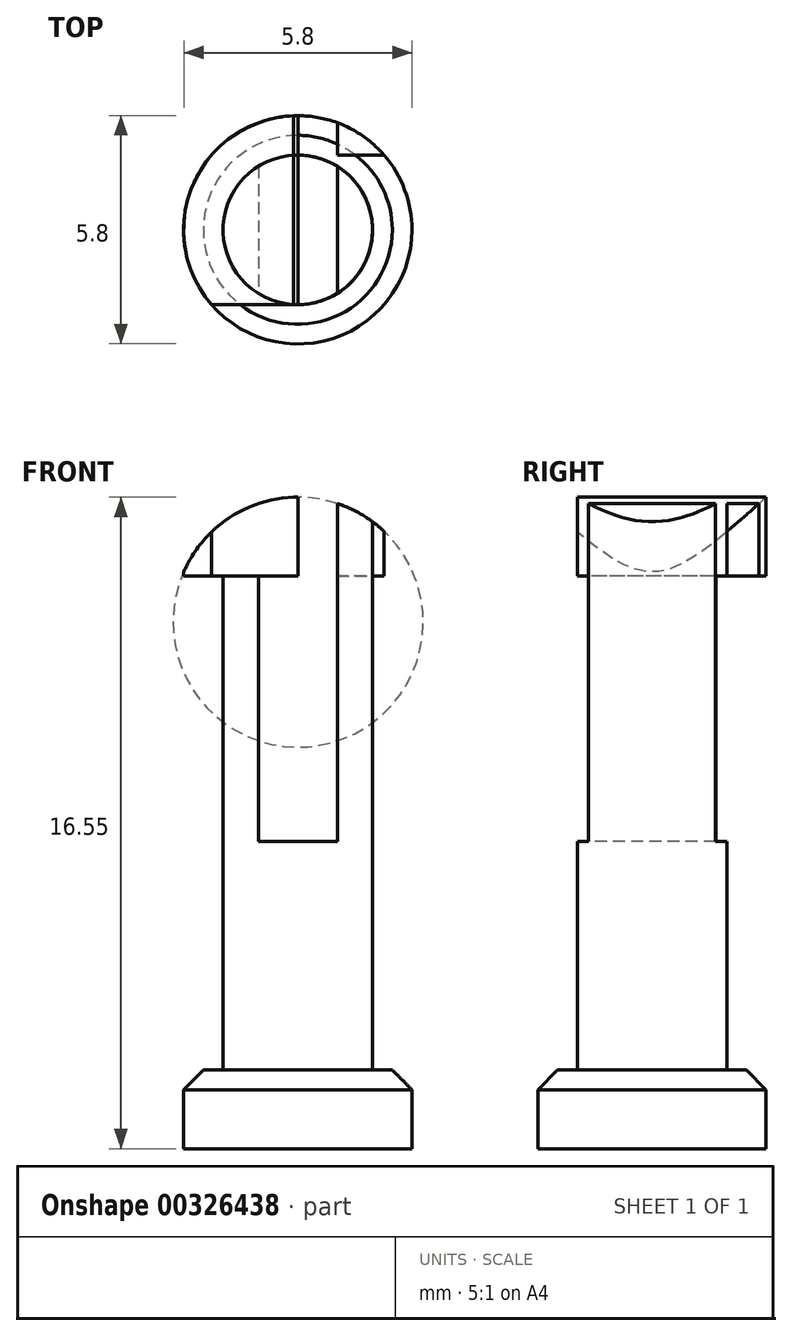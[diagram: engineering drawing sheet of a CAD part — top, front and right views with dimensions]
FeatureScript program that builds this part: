
annotation { "Feature Type Name" : "Feature", "Feature Type Description" : "" }
export const myFeature = defineFeature(function(context is Context, id is Id, definition is map)
    precondition{}
    {
        {
            var Q0;
            Q0=qCreatedBy(makeId("Top.planeOp"),FACE);
            var sketch = newSketch(context, id + "F0", { "sketchPlane" : qUnion([Q0])});
            skCircle(sketch, "E0", {"center": v(-52.06, 27.8) * mm, "radius": 2.9 * mm});
            skSolve(sketch);
        }
        {
            var Q0;
            Q0=makeQuery(id+"F0.imprint","IMPRINT",FACE,{"disambiguationData":[TD([[makeQuery(id+"F0.imprint","IMPRINT",EDGE,{"derivedFrom":sQuery(id+"F0.wireOp",EDGE,"E0")}),1.0]])]});
            extrude(context, id + "F1", {"entities" : qUnion([Q0]), "depth" : 2 * mm});
        }
        {
            var Q0;
            Q0=makeQuery(id+"F1.opExtrude","CAP_FACE",FACE,{"disambiguationData":[OSD([sQuery(id+"F0.wireOp",EDGE,"E0")])],"isStart":false});
            var sketch = newSketch(context, id + "F2", { "sketchPlane" : qUnion([Q0])});
            skPoint(sketch, "E1", {"position": v(-52.06, 27.8) * mm});
            skCircle(sketch, "E2", {"center": v(-52.06, 27.8) * mm, "radius": 1.9 * mm});
            skSolve(sketch);
        }
        {
            var Q0;
            Q0=makeQuery(id+"F2.imprint","IMPRINT",FACE,{"disambiguationData":[TD([[makeQuery(id+"F2.imprint","IMPRINT",EDGE,{"derivedFrom":sQuery(id+"F2.wireOp",EDGE,"E2")}),1.0]])]});
            var Q1;
            Q1=sQuery(id+"F2.wireOp",EDGE,"E2");
            extrude(context, id + "F3", {"entities" : qUnion([Q0]), "operationType" : NewBodyOperationType.ADD, "surfaceEntities" : qUnion([Q1]), "depth" : 12.55 * mm});
        }
        {
            var Q0;
            Q0=makeQuery(id+"F3.opExtrude","CAP_FACE",FACE,{"disambiguationData":[OSD([sQuery(id+"F2.wireOp",EDGE,"E2")])],"isStart":false});
            var sketch = newSketch(context, id + "F4", { "sketchPlane" : qUnion([Q0])});
            skPoint(sketch, "E3", {"position": v(-52.06, 27.8) * mm});
            skCircle(sketch, "E4", {"center": v(-52.06, 27.8) * mm, "radius": 2.9 * mm});
            skLineSegment(sketch, "E5", {"start": v(-52.06, 30.7) * mm, "end": v(-52.06, 24.9) * mm, "construction": true});
            skLineSegment(sketch, "E6", {"start": v(-52.06, 29.7) * mm, "end": v(-49.87, 29.7) * mm});
            skLineSegment(sketch, "E7", {"start": v(-49.87, 29.7) * mm, "end": v(-54.26, 29.7) * mm});
            skLineSegment(sketch, "E8", {"start": v(-52.06, 25.9) * mm, "end": v(-49.87, 25.9) * mm});
            skLineSegment(sketch, "E9", {"start": v(-49.87, 25.9) * mm, "end": v(-54.26, 25.9) * mm});
            skSolve(sketch);
        }
        {
            var Q0;
            {var subQ0=sQuery(id+"F4.wireOp",EDGE,"E7");var subQ1=sQuery(id+"F4.wireOp",EDGE,"E4");var subQ2=makeQuery(id+"F4.imprint","INTERSECT",VERTEX,{"disambiguationData":[OD(1.0)],"derivedFrom":[subQ1,subQ0]});Q0=makeQuery(id+"F4.imprint","IMPRINT",FACE,{"disambiguationData":[TD([[makeQuery(id+"F4.imprint","IMPRINT",EDGE,{"disambiguationData":[TD([[subQ2,-1.0]])],"derivedFrom":subQ1}),1.0]])]});}
            var Q1;
            {var subQ0=makeQuery(id+"F3.opExtrude","CAP_EDGE",EDGE,{"disambiguationData":[OSD([sQuery(id+"F2.wireOp",EDGE,"E2")])],"isStart":false});var subQ1=makeQuery(id+"F4.imprint","INTERSECT",VERTEX,{"derivedFrom":[subQ0,sQuery(id+"F4.wireOp",EDGE,"E7")]});Q1=makeQuery(id+"F4.imprint","IMPRINT",FACE,{"disambiguationData":[TD([[makeQuery(id+"F4.imprint","IMPRINT",EDGE,{"disambiguationData":[TD([[subQ1,-1.0]])],"derivedFrom":subQ0}),1.0]])]});}
            var Q2;
            {var subQ0=sQuery(id+"F4.wireOp",EDGE,"E7");var subQ1=sQuery(id+"F4.wireOp",EDGE,"E4");var subQ2=makeQuery(id+"F4.imprint","INTERSECT",VERTEX,{"disambiguationData":[OD(0.0)],"derivedFrom":[subQ1,subQ0]});Q2=makeQuery(id+"F4.imprint","IMPRINT",FACE,{"disambiguationData":[TD([[makeQuery(id+"F4.imprint","IMPRINT",EDGE,{"disambiguationData":[TD([[subQ2,1.0]])],"derivedFrom":subQ1}),1.0]])]});}
            extrude(context, id + "F5", {"entities" : qUnion([Q0, Q1, Q2]), "operationType" : NewBodyOperationType.ADD, "depth" : 2 * mm});
        }
        {
            var Q0;
            Q0=makeQuery(id+"F5.opExtrude","SWEPT_FACE",FACE,{"disambiguationData":[OSD([sQuery(id+"F4.wireOp",EDGE,"E9")])]});
            var sketch = newSketch(context, id + "F6", { "sketchPlane" : qUnion([Q0])});
            skLineSegment(sketch, "E10.bottom", {"start": v(-55, 16.55) * mm, "end": v(-49.1, 16.55) * mm});
            skLineSegment(sketch, "E10.top", {"start": v(-55, 14.55) * mm, "end": v(-53.06, 14.55) * mm});
            skLineSegment(sketch, "E10.left", {"start": v(-55, 16.55) * mm, "end": v(-55, 14.55) * mm});
            skLineSegment(sketch, "E10.right", {"start": v(-49.1, 16.55) * mm, "end": v(-49.1, 14.55) * mm});
            skPoint(sketch, "E11", {"position": v(-52.06, 16.55) * mm});
            skArc(sketch, "E12", {"start": v(-49.1, 14.55) * mm, "mid": v(-52.06, 16.55) * mm, "end": v(-55, 14.55) * mm});
            skPoint(sketch, "E13", {"position": v(-52.06, 2) * mm});
            skLineSegment(sketch, "E14", {"start": v(-52.06, 2) * mm, "end": v(-52.06, 14.55) * mm, "construction": true});
            skLineSegment(sketch, "E15.top", {"start": v(-53.06, 7.8) * mm, "end": v(-51.06, 7.8) * mm});
            skLineSegment(sketch, "E15.left", {"start": v(-53.06, 14.55) * mm, "end": v(-53.06, 7.8) * mm});
            skLineSegment(sketch, "E15.right", {"start": v(-51.06, 13.8) * mm, "end": v(-51.06, 7.8) * mm});
            skPoint(sketch, "E16", {"position": v(-52.06, 7.8) * mm});
            skLineSegment(sketch, "E17", {"start": v(-53.06, 14.55) * mm, "end": v(-53.06, 16.55) * mm});
            skLineSegment(sketch, "E18", {"start": v(-51.06, 13.8) * mm, "end": v(-51.06, 16.55) * mm});
            skLineSegment(sketch, "E19.trimOffspring", {"start": v(-51.06, 14.55) * mm, "end": v(-49.1, 14.55) * mm});
            skSolve(sketch);
        }
        {
            var Q0;
            {var subQ0=sQuery(id+"F6.wireOp",EDGE,"XV074B50-gbtO-xtoO-LmDx-LcEMkbkd0Xud.bottom");var subQ1=makeQuery(id+"F6.imprint","IMPRINT",VERTEX,{"derivedFrom":subQ0});var subQ4=sQuery(id+"F6.wireOp",EDGE,"E17");var subQ5=makeQuery(id+"F6.imprint","INTERSECT",VERTEX,{"derivedFrom":[subQ0,sQuery(id+"F6.wireOp",EDGE,"E15.left"),subQ4]});Q0=makeQuery(id+"F6.imprint","IMPRINT",FACE,{"disambiguationData":[TD([[makeQuery(id+"F6.imprint","IMPRINT",EDGE,{"disambiguationData":[TD([[subQ1,1.0],[subQ5,-1.0]])],"derivedFrom":subQ0}),1.0]])]});}
            var Q1;
            {var subQ0=sQuery(id+"F6.wireOp",EDGE,"E12");var subQ4=sQuery(id+"F6.wireOp",EDGE,"E17");var subQ5=makeQuery(id+"F6.imprint","INTERSECT",VERTEX,{"derivedFrom":[subQ0,subQ4]});Q1=makeQuery(id+"F6.imprint","IMPRINT",FACE,{"disambiguationData":[TD([[makeQuery(id+"F6.imprint","IMPRINT",EDGE,{"disambiguationData":[TD([[subQ5,1.0]])],"derivedFrom":subQ0}),-1.0]])]});}
            var Q2;
            {var subQ0=sQuery(id+"F6.wireOp",EDGE,"E18");var subQ1=sQuery(id+"F6.wireOp",EDGE,"E12");var subQ2=makeQuery(id+"F6.imprint","INTERSECT",VERTEX,{"derivedFrom":[subQ1,subQ0]});Q2=makeQuery(id+"F6.imprint","IMPRINT",FACE,{"disambiguationData":[TD([[makeQuery(id+"F6.imprint","IMPRINT",EDGE,{"disambiguationData":[TD([[subQ2,-1.0]])],"derivedFrom":subQ1}),-1.0]])]});}
            var Q3;
            {var subQ0=sQuery(id+"F6.wireOp",EDGE,"E18");var subQ1=sQuery(id+"F6.wireOp",EDGE,"E12");var subQ2=makeQuery(id+"F6.imprint","INTERSECT",VERTEX,{"derivedFrom":[subQ1,subQ0]});Q3=makeQuery(id+"F6.imprint","IMPRINT",FACE,{"disambiguationData":[TD([[makeQuery(id+"F6.imprint","IMPRINT",EDGE,{"disambiguationData":[TD([[subQ2,-1.0]])],"derivedFrom":subQ0}),-1.0]])]});}
            var Q4;
            {var subQ1=sQuery(id+"F6.wireOp",EDGE,"E10.right");Q4=makeQuery(id+"F6.imprint","IMPRINT",FACE,{"disambiguationData":[TD([[makeQuery(id+"F6.imprint","IMPRINT",EDGE,{"derivedFrom":subQ1}),-1.0]])]});}
            var Q5;
            {var subQ0=sQuery(id+"F6.wireOp",EDGE,"E17");var subQ1=sQuery(id+"F6.wireOp",EDGE,"E12");var subQ2=makeQuery(id+"F6.imprint","INTERSECT",VERTEX,{"derivedFrom":[subQ1,subQ0]});Q5=makeQuery(id+"F6.imprint","IMPRINT",FACE,{"disambiguationData":[TD([[makeQuery(id+"F6.imprint","IMPRINT",EDGE,{"disambiguationData":[TD([[subQ2,-1.0]])],"derivedFrom":subQ0}),1.0]])]});}
            var Q6;
            {var subQ7=sQuery(id+"F6.wireOp",EDGE,"E10.left");Q6=makeQuery(id+"F6.imprint","IMPRINT",FACE,{"disambiguationData":[TD([[makeQuery(id+"F6.imprint","IMPRINT",EDGE,{"derivedFrom":subQ7}),1.0]])]});}
            var Q7;
            Q7=makeQuery(id+"F6.imprint","IMPRINT",FACE,{"disambiguationData":[TD([[makeQuery(id+"F6.imprint","IMPRINT",EDGE,{"derivedFrom":sQuery(id+"F6.wireOp",EDGE,"E15.top")}),1.0]])]});
            var Q8;
            Q8=makeQuery(id+"F5.opExtrude","SWEPT_FACE",FACE,{"disambiguationData":[OSD([sQuery(id+"F4.wireOp",EDGE,"E7")])]});
            extrude(context, id + "F7", {"entities" : qUnion([Q0, Q1, Q2, Q3, Q4, Q5, Q6, Q7, Q8]), "operationType" : NewBodyOperationType.REMOVE, "oppositeDirection" : true, "depth" : 25 * mm});
        }
        {
            var Q0;
            Q0=makeQuery(id+"F1.opExtrude","CAP_EDGE",EDGE,{"disambiguationData":[OSD([sQuery(id+"F0.wireOp",EDGE,"E0")])],"isStart":false});
            chamfer(context, id + "F8", {"entities" : qUnion([Q0]), "width" : 0.5 * mm, "tangentPropagation" : true});
        }
        {
            var Q0;
            {var subQ13=sQuery(id+"F6.wireOp",EDGE,"E12");var subQ17=sQuery(id+"F6.wireOp",EDGE,"E18");var subQ18=makeQuery(id+"F6.imprint","INTERSECT",VERTEX,{"derivedFrom":[subQ13,subQ17]});Q0=makeQuery(id+"F6.imprint","IMPRINT",FACE,{"disambiguationData":[TD([[makeQuery(id+"F6.imprint","IMPRINT",EDGE,{"disambiguationData":[TD([[subQ18,-1.0]])],"derivedFrom":subQ13}),1.0]])]});}
            var Q1;
            Q1=makeQuery(id+"F6.imprint","IMPRINT",FACE,{"disambiguationData":[TD([[makeQuery(id+"F6.imprint","IMPRINT",EDGE,{"derivedFrom":sQuery(id+"F6.wireOp",EDGE,"E15.top")}),1.0]])]});
            extrude(context, id + "F9", {"entities" : qUnion([Q0, Q1]), "operationType" : NewBodyOperationType.REMOVE, "oppositeDirection" : true, "depth" : 25 * mm});
        }
    });
